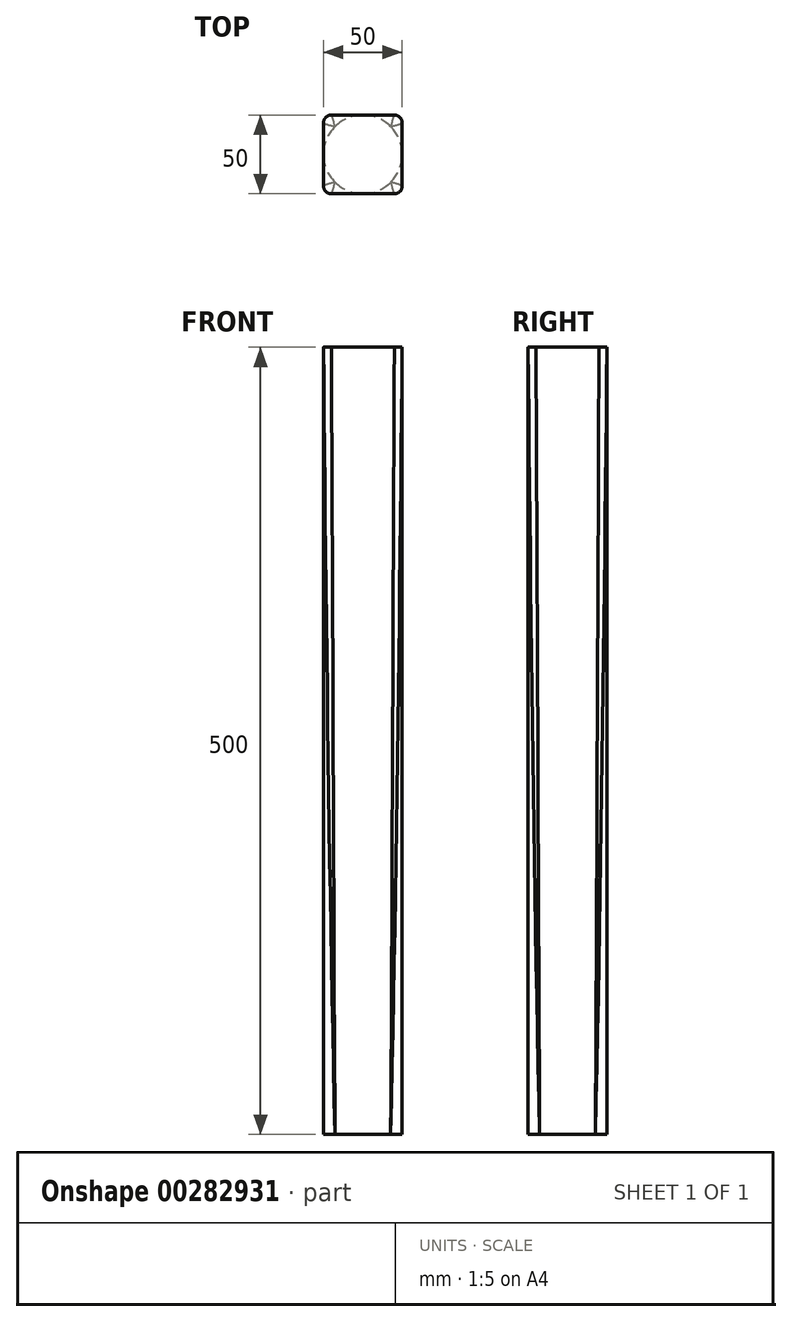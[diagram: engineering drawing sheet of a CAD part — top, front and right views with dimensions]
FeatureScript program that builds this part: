
annotation { "Feature Type Name" : "Feature", "Feature Type Description" : "" }
export const myFeature = defineFeature(function(context is Context, id is Id, definition is map)
    precondition{}
    {
        {
            var Q0;
            Q0=qCreatedBy(makeId("Top.planeOp"),FACE);
            var sketch = newSketch(context, id + "F0", { "sketchPlane" : qUnion([Q0])});
            skLineSegment(sketch, "E0.bottom", {"start": v(25, 25) * mm, "end": v(-25, 25) * mm});
            skLineSegment(sketch, "E0.top", {"start": v(25, -25) * mm, "end": v(-25, -25) * mm});
            skLineSegment(sketch, "E0.left", {"start": v(25, 25) * mm, "end": v(25, -25) * mm});
            skLineSegment(sketch, "E0.right", {"start": v(-25, 25) * mm, "end": v(-25, -25) * mm});
            skPoint(sketch, "E0.middle", {"position": v(0, 0) * mm});
            skSolve(sketch);
        }
        {
            var Q0;
            Q0=qCreatedBy(makeId("Top.planeOp"),FACE);
            cPlane(context, id + "F1", {"entities" : qUnion([Q0]), "cplaneType" : CPlaneType.OFFSET, "offset" : 500 * mm, "width" : 150 * mm, "height" : 150 * mm});
        }
        {
            var Q0;
            Q0=qCreatedBy(id+"F1.planeOp",FACE);
            var sketch = newSketch(context, id + "F2", { "sketchPlane" : qUnion([Q0])});
            skLineSegment(sketch, "E1.bottom", {"start": v(25, 25) * mm, "end": v(-25, 25) * mm});
            skLineSegment(sketch, "E1.top", {"start": v(25, -25) * mm, "end": v(-25, -25) * mm});
            skLineSegment(sketch, "E1.left", {"start": v(25, 25) * mm, "end": v(25, -25) * mm});
            skLineSegment(sketch, "E1.right", {"start": v(-25, 25) * mm, "end": v(-25, -25) * mm});
            skPoint(sketch, "E1.middle", {"position": v(0, 0) * mm});
            skSolve(sketch);
        }
        {
            var Q0;
            Q0=makeQuery(id+"F0.imprint","IMPRINT",FACE,{"disambiguationData":[TD([[makeQuery(id+"F0.imprint","IMPRINT",EDGE,{"derivedFrom":sQuery(id+"F0.wireOp",EDGE,"E0.bottom")}),1.0]])]});
            var sketch = newSketch(context, id + "F3", { "sketchPlane" : qUnion([Q0])});
            skCircle(sketch, "E2", {"center": v(0, 0) * mm, "radius": 25 * mm});
            skSolve(sketch);
        }
        {
            var Q0;
            {var subQ0=sQuery(id+"F3.wireOp",EDGE,"E2");var subQ1=makeQuery(id+"F3.imprint","INTERSECT",VERTEX,{"derivedFrom":[makeQuery(id+"F0.imprint","IMPRINT",EDGE,{"derivedFrom":sQuery(id+"F0.wireOp",EDGE,"E0.bottom")}),subQ0]});Q0=makeQuery(id+"F3.imprint","IMPRINT",FACE,{"disambiguationData":[TD([[makeQuery(id+"F3.imprint","IMPRINT",EDGE,{"disambiguationData":[TD([[subQ1,1.0]])],"derivedFrom":subQ0}),1.0]])]});}
            var Q1;
            Q1=makeQuery(id+"F2.imprint","IMPRINT",FACE,{"disambiguationData":[TD([[makeQuery(id+"F2.imprint","IMPRINT",EDGE,{"derivedFrom":sQuery(id+"F2.wireOp",EDGE,"E1.bottom")}),1.0]])]});
            loft(context, id + "F4", {"sheetProfilesArray" : [{ "sheetProfileEntities" : qUnion([Q0]) }, { "sheetProfileEntities" : qUnion([Q1]) }]});
        }
        {
            var Q0;
            Q0=makeQuery(id+"F4.opLoft","SWEPT_EDGE",EDGE,{"disambiguationData":[OSD([sQuery(id+"F0.wireOp",EDGE,"E0.left"),sQuery(id+"F2.wireOp",EDGE,"E1.bottom"),sQuery(id+"F2.wireOp",EDGE,"E1.left"),sQuery(id+"F3.wireOp",EDGE,"E2")])]});
            var Q1;
            Q1=makeQuery(id+"F4.opLoft","SWEPT_EDGE",EDGE,{"disambiguationData":[OSD([sQuery(id+"F0.wireOp",EDGE,"E0.bottom"),sQuery(id+"F2.wireOp",EDGE,"E1.bottom"),sQuery(id+"F2.wireOp",EDGE,"E1.right"),sQuery(id+"F3.wireOp",EDGE,"E2")])]});
            var Q2;
            Q2=makeQuery(id+"F4.opLoft","SWEPT_EDGE",EDGE,{"disambiguationData":[OSD([sQuery(id+"F0.wireOp",EDGE,"E0.top"),sQuery(id+"F2.wireOp",EDGE,"E1.top"),sQuery(id+"F2.wireOp",EDGE,"E1.left"),sQuery(id+"F3.wireOp",EDGE,"E2")])]});
            var Q3;
            Q3=makeQuery(id+"F4.opLoft","SWEPT_EDGE",EDGE,{"disambiguationData":[OSD([sQuery(id+"F0.wireOp",EDGE,"E0.right"),sQuery(id+"F2.wireOp",EDGE,"E1.top"),sQuery(id+"F2.wireOp",EDGE,"E1.right"),sQuery(id+"F3.wireOp",EDGE,"E2")])]});
            fillet(context, id + "F5", {"entities" : qUnion([Q0, Q1, Q2, Q3]), "radius" : 5 * mm, "tangentPropagation" : true, "allowEdgeOverflow" : false});
        }
    });
